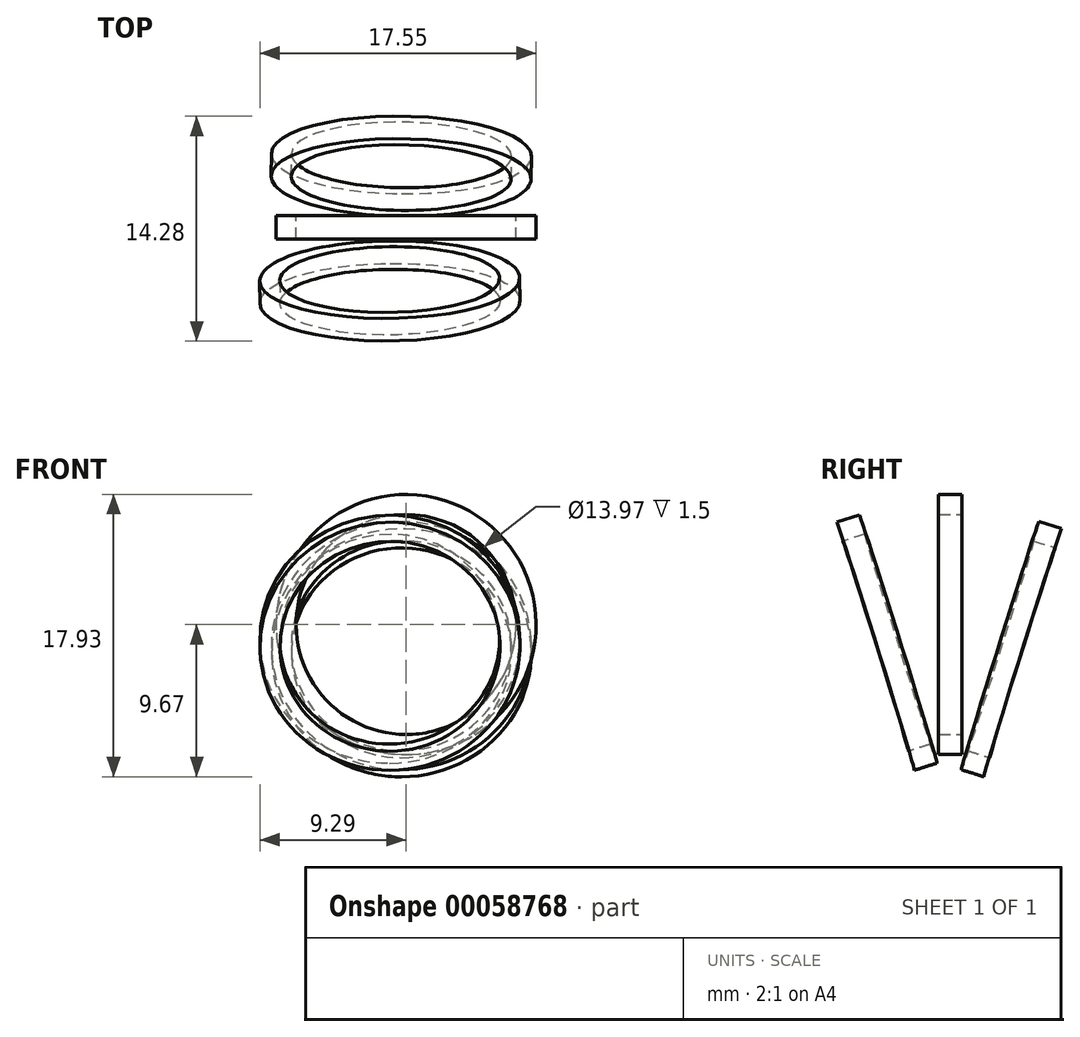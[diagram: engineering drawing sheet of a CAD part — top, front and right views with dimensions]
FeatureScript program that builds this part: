
annotation { "Feature Type Name" : "Feature", "Feature Type Description" : "" }
export const myFeature = defineFeature(function(context is Context, id is Id, definition is map)
    precondition{}
    {
        {
            var Q0;
            Q0=qCreatedBy(makeId("Right.planeOp"),FACE);
            var sketch = newSketch(context, id + "F0", { "sketchPlane" : qUnion([Q0])});
            skLineSegment(sketch, "E0", {"start": v(0, 0) * mm, "end": v(0, -16.51) * mm, "construction": true});
            skSolve(sketch);
        }
        {
            var Q0;
            Q0=qCreatedBy(makeId("Right.planeOp"),FACE);
            var sketch = newSketch(context, id + "F1", { "sketchPlane" : qUnion([Q0])});
            skLineSegment(sketch, "E1", {"start": v(0, -16.51) * mm, "end": v(28.99, 76.2) * mm});
            skLineSegment(sketch, "E2", {"start": v(0, -16.51) * mm, "end": v(-28.99, 76.2) * mm});
            skLineSegment(sketch, "E3", {"start": v(0, 76.2) * mm, "end": v(-28.99, 76.2) * mm, "construction": true});
            skLineSegment(sketch, "E4", {"start": v(0, 76.2) * mm, "end": v(28.99, 76.2) * mm, "construction": true});
            skSolve(sketch);
        }
        {
            var Q0;
            Q0=qCreatedBy(makeId("Front.planeOp"),FACE);
            var sketch = newSketch(context, id + "F2", { "sketchPlane" : qUnion([Q0])});
            skLineSegment(sketch, "E5", {"start": v(0, -17.04) * mm, "end": v(-14.3, -17.04) * mm, "construction": true});
            skSolve(sketch);
        }
        {
            var Q0;
            Q0=sQuery(id+"F1.wireOp",EDGE,"E2");
            var Q1;
            Q1=sQuery(id+"F2.wireOp",VERTEX,"E5.end");
            cPlane(context, id + "F3", {"entities" : qUnion([Q0, Q1]), "cplaneType" : CPlaneType.LINE_ANGLE, "offset" : 152.4 * mm, "angle" : 0 * degree, "width" : 152.4 * mm, "height" : 152.4 * mm});
        }
        {
            var Q0;
            Q0=sQuery(id+"F1.wireOp",EDGE,"E1");
            var Q1;
            Q1=sQuery(id+"F2.wireOp",VERTEX,"E5.end");
            cPlane(context, id + "F4", {"entities" : qUnion([Q0, Q1]), "cplaneType" : CPlaneType.LINE_ANGLE, "offset" : 152.4 * mm, "angle" : 0 * degree, "width" : 152.4 * mm, "height" : 152.4 * mm});
        }
        {
            var Q0;
            Q0=qCreatedBy(makeId("Front.planeOp"),FACE);
            var sketch = newSketch(context, id + "F5", { "sketchPlane" : qUnion([Q0])});
            skCircle(sketch, "E6", {"center": v(0, 0) * mm, "radius": 8.26 * mm});
            skCircle(sketch, "E7", {"center": v(0, 0) * mm, "radius": 6.99 * mm});
            skSolve(sketch);
        }
        {
            var Q0;
            Q0=qCreatedBy(id+"F4.planeOp",FACE);
            var sketch = newSketch(context, id + "F6", { "sketchPlane" : qUnion([Q0])});
            skCircle(sketch, "E8", {"center": v(-0.35, -0.34) * mm, "radius": 8.26 * mm});
            skCircle(sketch, "E9", {"center": v(-0.35, -0.34) * mm, "radius": 6.99 * mm});
            skSolve(sketch);
        }
        {
            var Q0;
            Q0=qCreatedBy(id+"F3.planeOp",FACE);
            var sketch = newSketch(context, id + "F7", { "sketchPlane" : qUnion([Q0])});
            skCircle(sketch, "E10", {"center": v(-1.08, 0.1) * mm, "radius": 8.26 * mm});
            skCircle(sketch, "E11", {"center": v(-1.08, 0.1) * mm, "radius": 6.99 * mm});
            skSolve(sketch);
        }
        {
            var Q0;
            Q0=makeQuery(id+"F7.imprint","IMPRINT",FACE,{"disambiguationData":[TD([[makeQuery(id+"F7.imprint","IMPRINT",EDGE,{"derivedFrom":sQuery(id+"F7.wireOp",EDGE,"E10")}),1.0]])]});
            extrude(context, id + "F8", {"entities" : qUnion([Q0]), "oppositeDirection" : true, "depth" : 1.5 * mm});
        }
        {
            var Q0;
            Q0=makeQuery(id+"F5.imprint","IMPRINT",FACE,{"disambiguationData":[TD([[makeQuery(id+"F5.imprint","IMPRINT",EDGE,{"derivedFrom":sQuery(id+"F5.wireOp",EDGE,"E6")}),1.0]])]});
            extrude(context, id + "F9", {"entities" : qUnion([Q0]), "endBound" : BoundingType.SYMMETRIC, "depth" : 1.5 * mm});
        }
        {
            var Q0;
            Q0=makeQuery(id+"F6.imprint","IMPRINT",FACE,{"disambiguationData":[TD([[makeQuery(id+"F6.imprint","IMPRINT",EDGE,{"derivedFrom":sQuery(id+"F6.wireOp",EDGE,"E8")}),1.0]])]});
            extrude(context, id + "F10", {"entities" : qUnion([Q0]), "depth" : 1.5 * mm});
        }
    });
